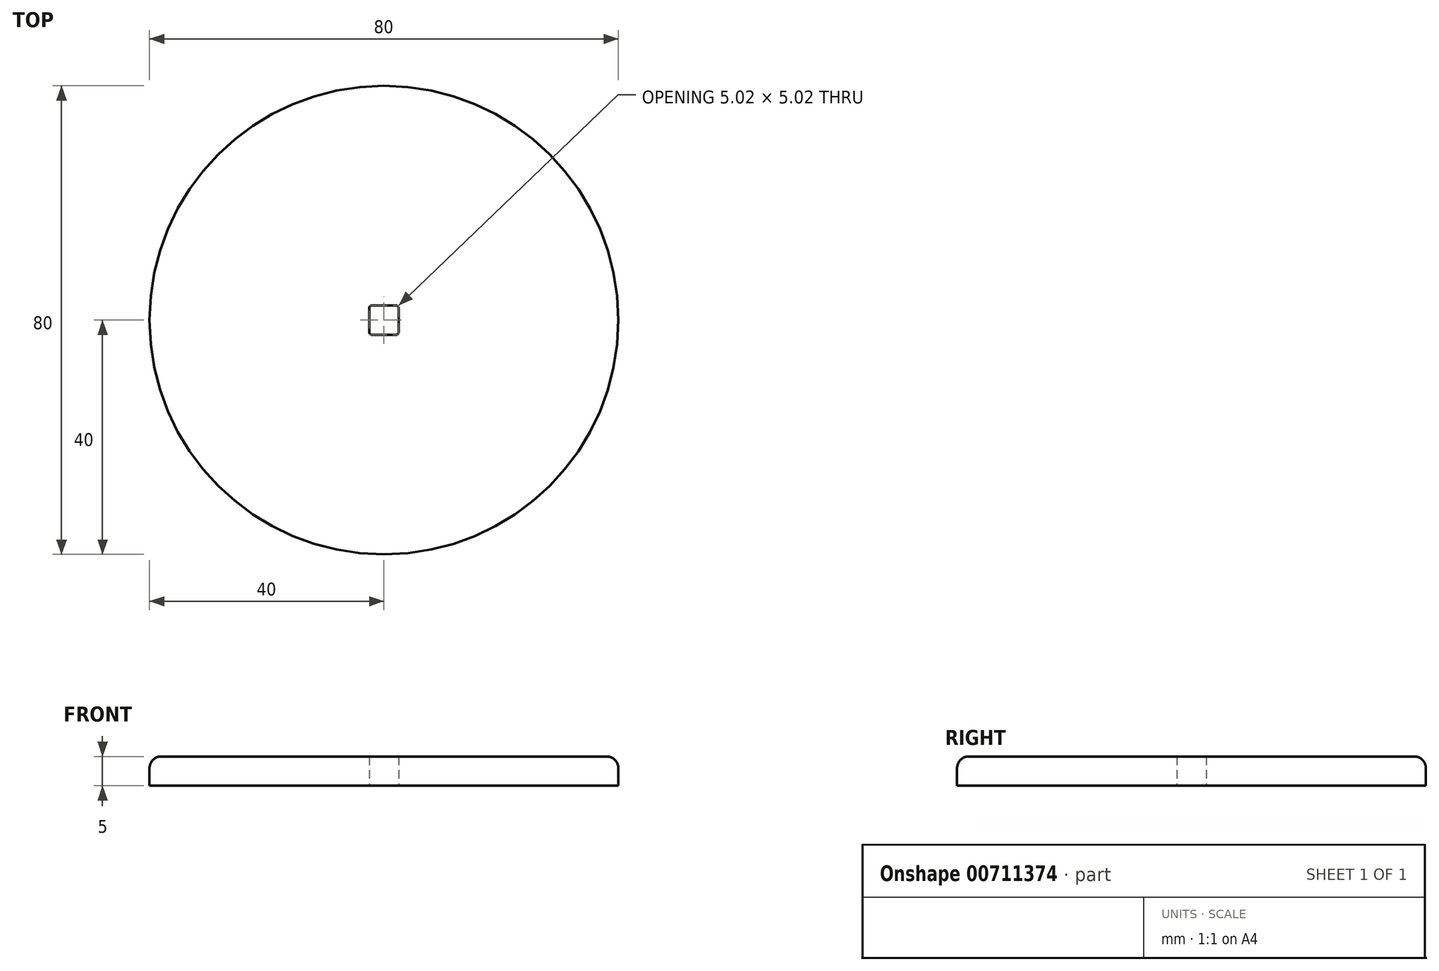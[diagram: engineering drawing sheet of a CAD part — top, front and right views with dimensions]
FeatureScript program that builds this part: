
annotation { "Feature Type Name" : "Feature", "Feature Type Description" : "" }
export const myFeature = defineFeature(function(context is Context, id is Id, definition is map)
    precondition{}
    {
        {
            var Q0;
            Q0=qCreatedBy(makeId("Top.planeOp"),FACE);
            var sketch = newSketch(context, id + "F0", { "sketchPlane" : qUnion([Q0])});
            skCircle(sketch, "E0", {"center": v(0, 0) * mm, "radius": 40 * mm});
            skLineSegment(sketch, "E1.bottom", {"start": v(2.5, 2.5) * mm, "end": v(-2.5, 2.5) * mm});
            skLineSegment(sketch, "E1.top", {"start": v(2.5, -2.5) * mm, "end": v(-2.51, -2.5) * mm});
            skLineSegment(sketch, "E1.left", {"start": v(2.5, 2.5) * mm, "end": v(2.5, -2.51) * mm});
            skLineSegment(sketch, "E1.right", {"start": v(-2.5, 2.5) * mm, "end": v(-2.51, -2.51) * mm});
            skSolve(sketch);
        }
        {
            var Q0;
            Q0 = qSketchRegion(id + "F0", true);
            extrude(context, id + "F1", {"entities" : qUnion([Q0]), "depth" : 5 * mm, "offsetDistance" : 25 * mm});
        }
        {
            var Q0;
            Q0=makeQuery(id+"F1.opExtrude","SWEPT_EDGE",EDGE,{"disambiguationData":[OSD([sQuery(id+"F0.wireOp",EDGE,"E1.bottom"),sQuery(id+"F0.wireOp",EDGE,"E1.right")])]});
            var Q1;
            Q1=makeQuery(id+"F1.opExtrude","SWEPT_EDGE",EDGE,{"disambiguationData":[OSD([sQuery(id+"F0.wireOp",EDGE,"E1.top"),sQuery(id+"F0.wireOp",EDGE,"E1.right")])]});
            var Q2;
            Q2=makeQuery(id+"F1.opExtrude","SWEPT_EDGE",EDGE,{"disambiguationData":[OSD([sQuery(id+"F0.wireOp",EDGE,"E1.top"),sQuery(id+"F0.wireOp",EDGE,"E1.left")])]});
            var Q3;
            Q3=makeQuery(id+"F1.opExtrude","SWEPT_EDGE",EDGE,{"disambiguationData":[OSD([sQuery(id+"F0.wireOp",EDGE,"E1.bottom"),sQuery(id+"F0.wireOp",EDGE,"E1.left")])]});
            fillet(context, id + "F2", {"entities" : qUnion([Q0, Q1, Q2, Q3]), "radius" : 0.45 * mm, "tangentPropagation" : true, "allowEdgeOverflow" : false});
        }
        {
            var Q0;
            Q0=makeQuery(id+"F1.opExtrude","CAP_EDGE",EDGE,{"disambiguationData":[OSD([sQuery(id+"F0.wireOp",EDGE,"E0")])],"isStart":false});
            fillet(context, id + "F3", {"entities" : qUnion([Q0]), "radius" : 2 * mm, "tangentPropagation" : true, "allowEdgeOverflow" : false});
        }
    });
